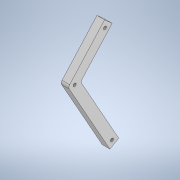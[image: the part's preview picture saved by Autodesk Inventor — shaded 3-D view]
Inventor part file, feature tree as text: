
AUTODESK INVENTOR PART (.ipt)
format: ipt  version: 2020 (Build 240168000, 168)  size: 145,920 bytes
history: native  units: in
note: dims shown in document units (in); Inventor stores cm internally (conversion verified against a paired STEP export)
features: extrude x2, sketch x2
ambient origin geometry x8: Origin, YZ Plane, XZ Plane, XY Plane, X Axis, Y Axis, Z Axis, Center Point
bodies: Solid1 (feature_tree)
feature tree (4):
  extrude  "Extrusion1"  Depth=0.5906in TaperAngle=0.0deg
  extrude  "Extrusion2"  Depth=0.3937in
  sketch  "Sketch1"  dims[d0=0.7874in d1=6.2992in d2=0.7874in d3=0.3937in d4=0.7874in d5=3.937in d6=0.3937in d7=0.7874in d8=0.2362in d9=0.2362in d10=0.2362in d11=0.2362in d12=0.5906in d13=0.0in]
  sketch  "Sketch2"  dims[d14=0.2756in d15=0.2756in d16=0.3937in d17=0.3937in d18=0.2362in d19=0.2362in d20=0.3937in d21=0.3937in d22=0.2362in d23=0.3937in d24=0.3937in d25=0.0in d26=0.0in d27=0.7463in d28=0.3932in d29=8.037in d30=4.5513in]
